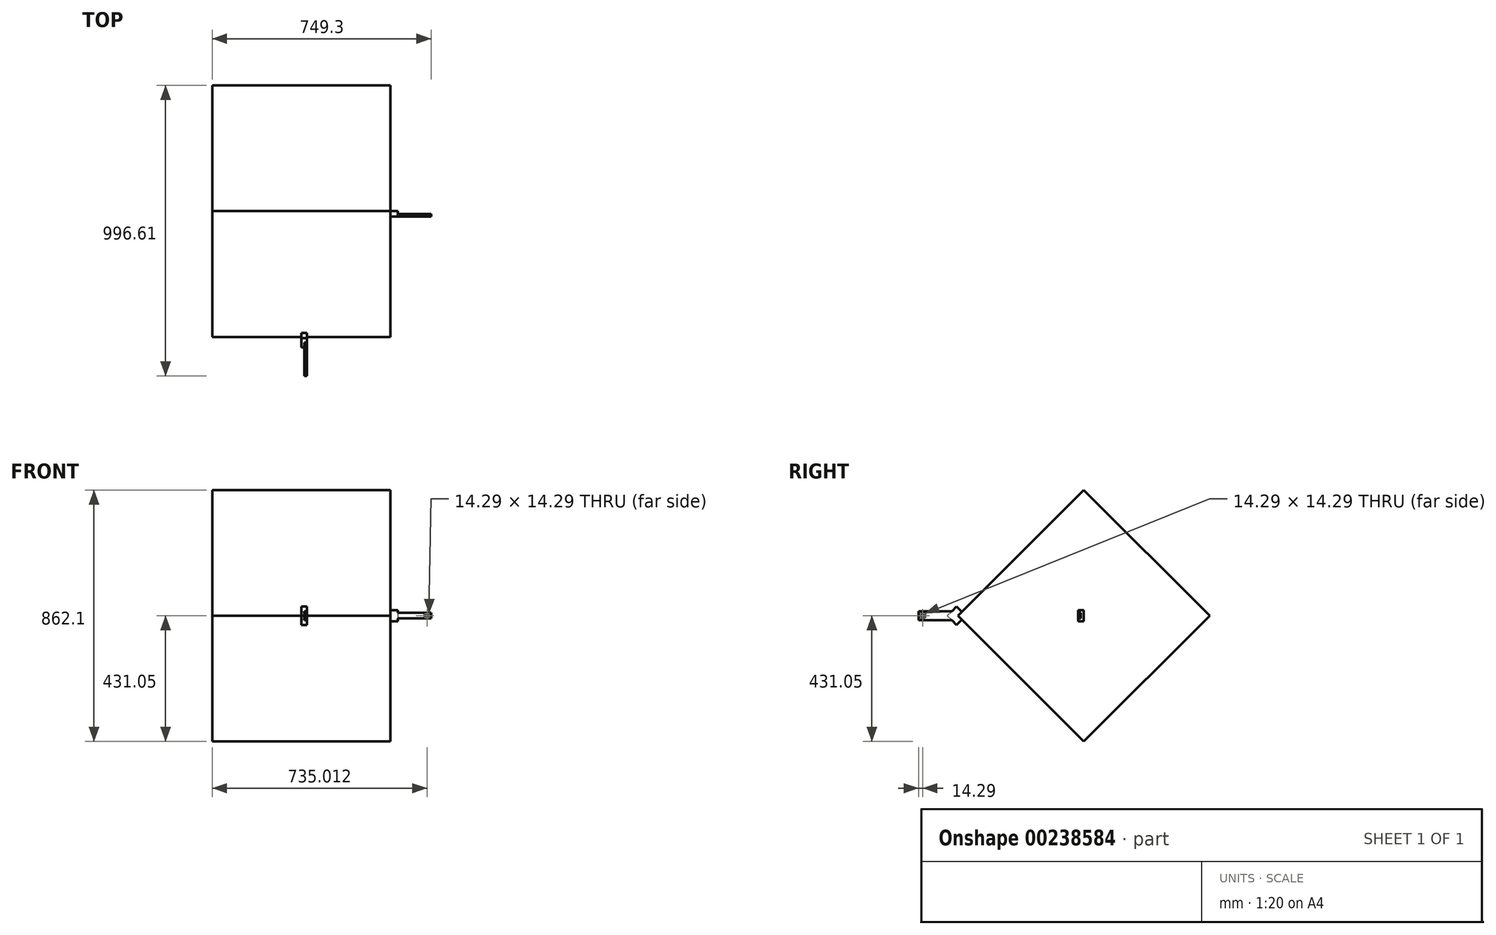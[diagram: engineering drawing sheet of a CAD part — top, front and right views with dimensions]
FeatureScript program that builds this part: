
annotation { "Feature Type Name" : "Feature", "Feature Type Description" : "" }
export const myFeature = defineFeature(function(context is Context, id is Id, definition is map)
    precondition{}
    {
        {
            assignVariable(context, id + "F0", {"name" : "length", "anyValue" : 609.6 * mm});
        }
        {
            var Q0;
            Q0=qCreatedBy(makeId("Top.planeOp"),FACE);
            var sketch = newSketch(context, id + "F1", { "sketchPlane" : qUnion([Q0])});
            skLineSegment(sketch, "E0.bottom", {"start": v(304.8, 304.8) * mm, "end": v(-304.8, 304.8) * mm});
            skLineSegment(sketch, "E0.top", {"start": v(304.8, -304.8) * mm, "end": v(-304.8, -304.8) * mm});
            skLineSegment(sketch, "E0.left", {"start": v(304.8, 304.8) * mm, "end": v(304.8, -304.8) * mm});
            skLineSegment(sketch, "E0.right", {"start": v(-304.8, 304.8) * mm, "end": v(-304.8, -304.8) * mm});
            skPoint(sketch, "E0.middle", {"position": v(0, 0) * mm});
            skSolve(sketch);
        }
        {
            var Q0;
            Q0 = qSketchRegion(id + "F1", true);
            extrude(context, id + "F2", {"entities" : qUnion([Q0]), "endBound" : BoundingType.SYMMETRIC, "oppositeDirection" : true, "depth" : getVariable(context, 'length'), "offsetDistance" : 25.4 * mm});
        }
        {
            assignVariable(context, id + "F3", {"name" : "gripThickness", "anyValue" : 25.4 * mm});
        }
        {
            var Q0;
            Q0=qCreatedBy(makeId("Top.planeOp"),FACE);
            var sketch = newSketch(context, id + "F4", { "sketchPlane" : qUnion([Q0])});
            skLineSegment(sketch, "E1", {"start": v(0, 0) * mm, "end": v(1252.23, 0) * mm});
            skSolve(sketch);
        }
        {
            var Q0;
            Q0=makeQuery(id+"F2.opExtrude","SWEPT_BODY",BODY,{"disambiguationData":[OSD([sQuery(id+"F1.wireOp",EDGE,"E0.bottom"),sQuery(id+"F1.wireOp",EDGE,"E0.top"),sQuery(id+"F1.wireOp",EDGE,"E0.left"),sQuery(id+"F1.wireOp",EDGE,"E0.right")])]});
            var Q1;
            Q1=sQuery(id+"F4.wireOp",EDGE,"E1");
            transform(context, id + "F5", {"entities" : qUnion([Q0]), "transformType" : TransformType.ROTATION, "transformAxis" : qUnion([Q1]), "angle" : 45 * degree, "makeCopy" : false});
        }
        {
            var Q0;
            Q0=makeQuery(id+"F2.opExtrude","CAP_FACE",FACE,{"disambiguationData":[OSD([sQuery(id+"F1.wireOp",EDGE,"E0.bottom"),sQuery(id+"F1.wireOp",EDGE,"E0.top"),sQuery(id+"F1.wireOp",EDGE,"E0.left"),sQuery(id+"F1.wireOp",EDGE,"E0.right")])],"isStart":true});
            var sketch = newSketch(context, id + "F6", { "sketchPlane" : qUnion([Q0])});
            skLineSegment(sketch, "E2", {"start": v(0, -304.8) * mm, "end": v(19.05, -304.8) * mm});
            skLineSegment(sketch, "E3", {"start": v(19.05, -304.8) * mm, "end": v(19.05, -285.75) * mm});
            skLineSegment(sketch, "E4", {"start": v(0, -304.8) * mm, "end": v(-19.05, -304.8) * mm});
            skLineSegment(sketch, "E5", {"start": v(-19.05, -304.8) * mm, "end": v(-19.05, -285.75) * mm});
            skLineSegment(sketch, "E6", {"start": v(-19.05, -285.75) * mm, "end": v(19.05, -285.75) * mm});
            skLineSegment(sketch, "E7", {"start": v(0, -285.75) * mm, "end": v(0, -304.8) * mm});
            skSolve(sketch);
        }
        {
            var Q0;
            Q0=makeQuery(id+"F6.imprint","IMPRINT",FACE,{"disambiguationData":[TD([[makeQuery(id+"F6.imprint","IMPRINT",EDGE,{"derivedFrom":sQuery(id+"F6.wireOp",EDGE,"E2")}),-1.0]])]});
            extrude(context, id + "F7", {"entities" : qUnion([Q0]), "depth" : getVariable(context, 'gripThickness'), "offsetDistance" : 25.4 * mm});
        }
        {
            var Q0;
            Q0=makeQuery(id+"F2.opExtrude","SWEPT_FACE",FACE,{"disambiguationData":[OSD([sQuery(id+"F1.wireOp",EDGE,"E0.top")])]});
            var sketch = newSketch(context, id + "F8", { "sketchPlane" : qUnion([Q0])});
            skLineSegment(sketch, "E8.0.1", {"start": v(19.05, 304.8) * mm, "end": v(19.05, 330.2) * mm});
            skLineSegment(sketch, "E8.0.2", {"start": v(19.05, 330.2) * mm, "end": v(19.05, 330.2) * mm});
            skLineSegment(sketch, "E8.0.3", {"start": v(19.05, 304.8) * mm, "end": v(19.05, 330.2) * mm});
            skLineSegment(sketch, "E9", {"start": v(19.05, 304.8) * mm, "end": v(19.05, 285.75) * mm});
            skLineSegment(sketch, "E10", {"start": v(19.05, 285.75) * mm, "end": v(19.05, 285.75) * mm});
            skLineSegment(sketch, "E11", {"start": v(0, 304.8) * mm, "end": v(0, 330.2) * mm});
            skLineSegment(sketch, "E12", {"start": v(19.05, 330.2) * mm, "end": v(0, 330.2) * mm});
            skLineSegment(sketch, "E13", {"start": v(19.05, 285.75) * mm, "end": v(0, 285.75) * mm});
            skLineSegment(sketch, "E14", {"start": v(0, 285.75) * mm, "end": v(0, 304.8) * mm});
            skSolve(sketch);
        }
        {
            var Q0;
            {var subQ0=sQuery(id+"F8.wireOp",EDGE,"E8.0.1");Q0=makeQuery(id+"F8.imprint","IMPRINT",FACE,{"disambiguationData":[TD([[makeQuery(id+"F8.imprint","IMPRINT",EDGE,{"derivedFrom":subQ0}),1.0]])]});}
            var Q1;
            {var subQ0=sQuery(id+"F8.wireOp",EDGE,"E9");Q1=makeQuery(id+"F8.imprint","IMPRINT",FACE,{"disambiguationData":[TD([[makeQuery(id+"F8.imprint","IMPRINT",EDGE,{"derivedFrom":subQ0}),-1.0]])]});}
            var Q2;
            {var subQ0=sQuery(id+"F8.wireOp",EDGE,"E8.0.3");Q2=makeQuery(id+"F8.imprint","IMPRINT",FACE,{"disambiguationData":[TD([[makeQuery(id+"F8.imprint","IMPRINT",EDGE,{"derivedFrom":subQ0}),1.0]])]});}
            extrude(context, id + "F9", {"entities" : qUnion([Q0, Q1, Q2]), "operationType" : NewBodyOperationType.ADD, "depth" : getVariable(context, 'gripThickness'), "offsetDistance" : 25.4 * mm});
        }
        {
            var Q0;
            Q0=makeQuery(id+"F2.opExtrude","SWEPT_FACE",FACE,{"disambiguationData":[OSD([sQuery(id+"F1.wireOp",EDGE,"E0.left")])]});
            var sketch = newSketch(context, id + "F10", { "sketchPlane" : qUnion([Q0])});
            skLineSegment(sketch, "E15.bottom", {"start": v(19.05, 19.05) * mm, "end": v(-19.05, 19.05) * mm});
            skLineSegment(sketch, "E15.top", {"start": v(19.05, -19.05) * mm, "end": v(-19.05, -19.05) * mm});
            skLineSegment(sketch, "E15.left", {"start": v(19.05, 19.05) * mm, "end": v(19.05, -19.05) * mm});
            skLineSegment(sketch, "E15.right", {"start": v(-19.05, 19.05) * mm, "end": v(-19.05, -19.05) * mm});
            skPoint(sketch, "E15.middle", {"position": v(0, 0) * mm});
            skLineSegment(sketch, "E16", {"start": v(0, 19.05) * mm, "end": v(0, 0) * mm});
            skLineSegment(sketch, "E17", {"start": v(0, -19.05) * mm, "end": v(0, 0) * mm});
            skSolve(sketch);
        }
        {
            var Q0;
            {var subQ0=sQuery(id+"F10.wireOp",EDGE,"E15.right");Q0=makeQuery(id+"F10.imprint","IMPRINT",FACE,{"disambiguationData":[TD([[makeQuery(id+"F10.imprint","IMPRINT",EDGE,{"derivedFrom":subQ0}),1.0]])]});}
            extrude(context, id + "F11", {"entities" : qUnion([Q0]), "depth" : getVariable(context, 'gripThickness'), "offsetDistance" : 25.4 * mm});
        }
        {
            var Q0;
            Q0=makeQuery(id+"F9.boolean.opBoolean","MERGE",FACE,{"derivedFrom":[makeQuery(id+"F7.opExtrude","SWEPT_FACE",FACE,{"disambiguationData":[OSD([sQuery(id+"F6.wireOp",EDGE,"E3")])]}),makeQuery(id+"F9.opExtrude","SWEPT_FACE",FACE,{"disambiguationData":[OSD([sQuery(id+"F8.wireOp",EDGE,"E8.0.1"),sQuery(id+"F8.wireOp",EDGE,"E9")])]})]});
            var sketch = newSketch(context, id + "F12", { "sketchPlane" : qUnion([Q0])});
            skLineSegment(sketch, "E18", {"start": v(-451.26, -15.72) * mm, "end": v(-565.56, -15.72) * mm});
            skLineSegment(sketch, "E19", {"start": v(-451.26, 15.72) * mm, "end": v(-565.56, 15.72) * mm});
            skLineSegment(sketch, "E20", {"start": v(-565.56, 15.72) * mm, "end": v(-565.56, -15.72) * mm});
            skLineSegment(sketch, "E21.bottom", {"start": v(-544.13, 7.14) * mm, "end": v(-558.41, 7.14) * mm});
            skLineSegment(sketch, "E21.top", {"start": v(-544.13, -7.14) * mm, "end": v(-558.41, -7.14) * mm});
            skLineSegment(sketch, "E21.left", {"start": v(-544.13, 7.14) * mm, "end": v(-544.13, -7.14) * mm});
            skLineSegment(sketch, "E21.right", {"start": v(-558.41, 7.14) * mm, "end": v(-558.41, -7.14) * mm});
            skPoint(sketch, "E21.middle", {"position": v(-551.27, 0) * mm});
            skPoint(sketch, "E22", {"position": v(-565.56, 0) * mm});
            skSolve(sketch);
        }
        {
            var Q0;
            {var subQ1=sQuery(id+"F12.wireOp",EDGE,"E18");Q0=makeQuery(id+"F12.imprint","IMPRINT",FACE,{"disambiguationData":[TD([[makeQuery(id+"F12.imprint","IMPRINT",EDGE,{"derivedFrom":subQ1}),-1.0]])]});}
            extrude(context, id + "F13", {"entities" : qUnion([Q0]), "operationType" : NewBodyOperationType.ADD, "oppositeDirection" : true, "depth" : getVariable(context, 'gripThickness') / 3, "offsetDistance" : 25.4 * mm});
        }
        {
            var Q0;
            Q0=makeQuery(id+"F11.opExtrude","SWEPT_FACE",FACE,{"disambiguationData":[OSD([sQuery(id+"F10.wireOp",EDGE,"E15.right")])]});
            var sketch = newSketch(context, id + "F14", { "sketchPlane" : qUnion([Q0])});
            skLineSegment(sketch, "E23", {"start": v(330.2, 19.05) * mm, "end": v(330.2, 0) * mm});
            skLineSegment(sketch, "E24", {"start": v(330.2, 0) * mm, "end": v(330.2, -19.05) * mm});
            skLineSegment(sketch, "E25", {"start": v(330.2, -9.53) * mm, "end": v(444.5, -9.53) * mm});
            skLineSegment(sketch, "E26", {"start": v(330.2, 9.53) * mm, "end": v(444.5, 9.53) * mm});
            skLineSegment(sketch, "E27", {"start": v(444.5, 9.53) * mm, "end": v(444.5, -9.53) * mm});
            skPoint(sketch, "E28", {"position": v(444.5, 0) * mm});
            skLineSegment(sketch, "E29.bottom", {"start": v(423.07, 7.14) * mm, "end": v(437.36, 7.14) * mm});
            skLineSegment(sketch, "E29.top", {"start": v(423.07, -7.14) * mm, "end": v(437.36, -7.14) * mm});
            skLineSegment(sketch, "E29.left", {"start": v(423.07, 7.14) * mm, "end": v(423.07, -7.14) * mm});
            skLineSegment(sketch, "E29.right", {"start": v(437.36, 7.14) * mm, "end": v(437.36, -7.14) * mm});
            skPoint(sketch, "E29.middle", {"position": v(430.21, 0) * mm});
            skSolve(sketch);
        }
        {
            var Q0;
            {var subQ1=sQuery(id+"F14.wireOp",EDGE,"E25");Q0=makeQuery(id+"F14.imprint","IMPRINT",FACE,{"disambiguationData":[TD([[makeQuery(id+"F14.imprint","IMPRINT",EDGE,{"derivedFrom":subQ1}),1.0]])]});}
            extrude(context, id + "F15", {"entities" : qUnion([Q0]), "operationType" : NewBodyOperationType.ADD, "oppositeDirection" : true, "depth" : getVariable(context, 'gripThickness') / 3, "offsetDistance" : 25.4 * mm});
        }
    });
